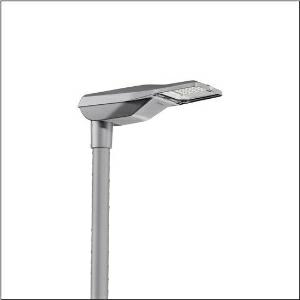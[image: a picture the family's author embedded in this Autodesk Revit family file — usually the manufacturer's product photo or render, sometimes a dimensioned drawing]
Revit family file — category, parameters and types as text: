
# Revit family: streetlight_sl_21_iq_micro___st1_0a_5xe1d41g08cb_d625
name_source: partatom
category: Lighting Fixtures
units: mm (PartAtom-declared; Revit-internal decimal feet)

## family parameters
Cut with Voids When Loaded = No
Host = Face
Light Source = No
Part Type = Normal
Room Calculation Point = No
Round Connector Dimension = Use Diameter
Shared = No

## types (1)
- --- (1 x LED, 2980 lm, 19.4 W, 4000K)
    Apparent Load = 19 VA
    CIE Flux Codes = 37 72 97 100 100
    Color Rendering = 70
    Color Temperature = 4000K
    Default Elevation = 1800 mm
    Description = Streetlight SL 21 iQ micro, mast luminaire, primary light control with lens, of PMMA, primary optical cover: cover, of toughened safety glass, transparent, light distribution: ST1.0a, light emission: direct distribution, primary light characteristic: asymmetric, installation type: post-top, side-entry, LED, High Power LED, rated luminous flux: 2.980lm, luminous efficacy: 154lm/W, light colour: 740, colour temperature: 4000K, control gear: iQ Street-Remote, control: Street-Remote, Auto-Match, Temp-Guard, Lumen-Switch, Night-Set, Smart-Wire, Light-Fading, Desk-Remote (wireless, voltage-free reading and setting of iQ features in the workshop via application-optimized NFC function/RFID function), optimised constant luminous flux control (CLO 2.0), pre-setting: linear dimming characteristic, mains connection: 220..240V, AC, 50/60Hz, start of lifetime: 19W, end of service life: 20W, reduction: 10W, luminaire housing, of diecast aluminium, powder-coated, SITECO metallic grey (DB 702S), corrosivity category C5 high according to DIN EN ISO 12944, please order mast flange separately, inclination adjustable: 0°, 5°, 10°, 15°, sealing non-destructively replaceable, multi-level sealing system, length: 528mm, width: 235mm, height: 110mm, mast flange for spigot size: 42mm (side-entry): 5XC10008XM4, 60/48mm (side-entry/post-top): 5XC10108XM2, 76/60mm (side-entry/post-top): 5XC10108XM1, protection rating (complete): IP66, insulation class (complete): insulation class II (safety insulation), certification: CE, ENEC, ENEC+, VDE, impact resistance: IK10, permissible operating ambient temperature for outdoor applications: -40..+50°C, standard-compliant lighting for roads and squares, packaging unit: 1 piece

Light Distribution: ST1.0a
    Height = 110 mm
    Lamp = 1 x LED
    Lamp Light Flux = 2980 lm
    Lamp Power = 19.4 W
    Lamp count = 1
    Length = 528 mm
    Luminous efficacy = 154 lm/W
    Manufacturer = Siteco
    ModVariant = No
    Model = 5XE1D41G08CB
    Number of Poles = 1
    OnlyDefault = Yes
    Power Factor = 1
    Product Name = Streetlight SL 21 iQ micro | ST1.0a
    Product group = mast luminaire | pylon top
    ProductGroupID = 6100
    Protection Class = Protection class II
    Protection Degree = IP 66
    RLX_Detail_Level = 1
    RLX_Emergency_Light_Flux = 0 lm
    RLX_Emergency_Type = 0
    RLX_Emergency_Type_DB = No
    RlxData = <blob elided: 98833 chars, md5=b5685de2>
    Socket = socket
    Standby Power = 0 W
    System Light Flux = 2980 lm
    System Power = 19 W
    Type Comments = factory setting: luminous flux: 100 % | dim-lin: 254 | 387 mA
    Type Image = l_1006881.jpg
    URL = http://relux.com
    VarID = @adj_138675
    Voltage = 0 V
    Weight = 0.00 kg
    Width = 235 mm

## geometry (parser evidence)
native form markers: Blend x4, Sweep x11
no freeform markers — native parametric forms only
